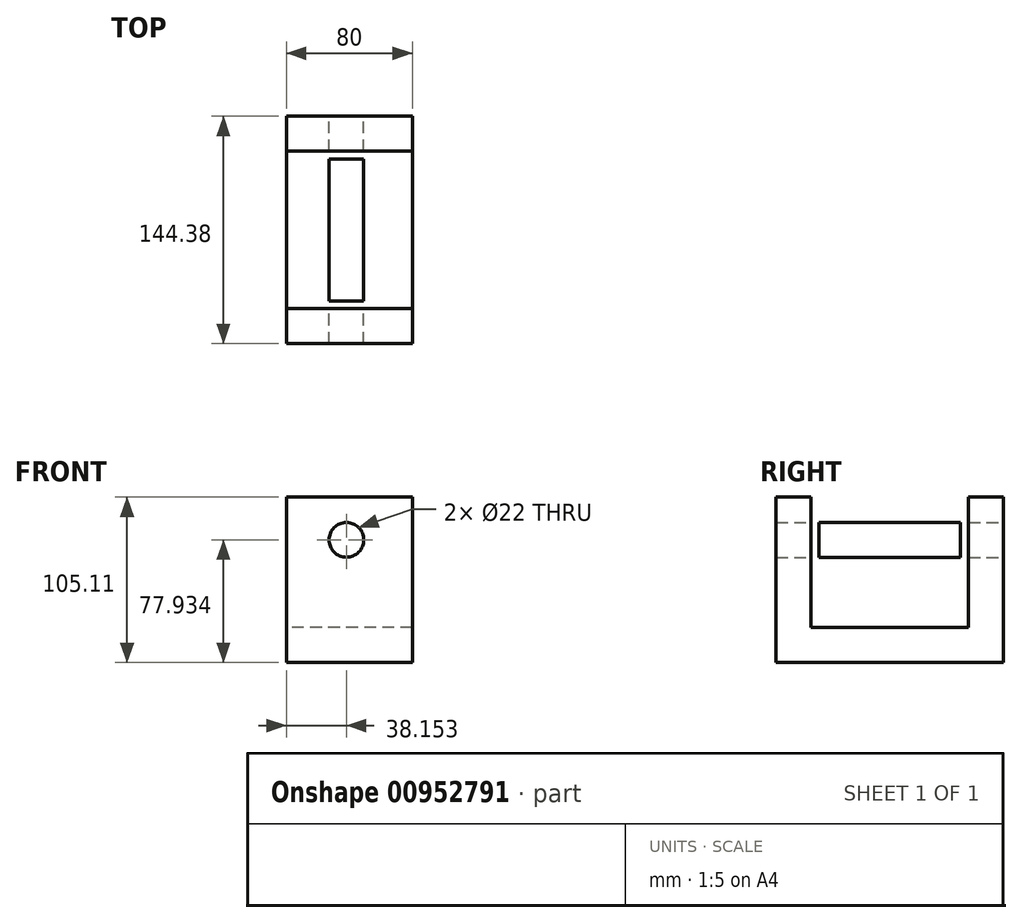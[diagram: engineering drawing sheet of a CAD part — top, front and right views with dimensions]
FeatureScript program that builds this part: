
annotation { "Feature Type Name" : "Feature", "Feature Type Description" : "" }
export const myFeature = defineFeature(function(context is Context, id is Id, definition is map)
    precondition{}
    {
        {
            var Q0;
            Q0=qCreatedBy(makeId("Right.planeOp"),FACE);
            var sketch = newSketch(context, id + "F0", { "sketchPlane" : qUnion([Q0])});
            skLineSegment(sketch, "E0", {"start": v(0, 0) * mm, "end": v(0, 85.7) * mm, "construction": true});
            skLineSegment(sketch, "E1", {"start": v(-50, 50.82) * mm, "end": v(-50, -32.1) * mm});
            skLineSegment(sketch, "E2.MirrorCS", {"start": v(50, 50.82) * mm, "end": v(50, -32.1) * mm});
            skLineSegment(sketch, "E3", {"start": v(-50, -32.1) * mm, "end": v(50, -32.1) * mm});
            skLineSegment(sketch, "E4.0", {"start": v(72.19, 50.82) * mm, "end": v(72.19, -54.3) * mm});
            skLineSegment(sketch, "E4.1", {"start": v(-72.19, -54.3) * mm, "end": v(72.19, -54.3) * mm});
            skLineSegment(sketch, "E4.2", {"start": v(-72.19, 50.82) * mm, "end": v(-72.19, -54.3) * mm});
            skLineSegment(sketch, "E5", {"start": v(-50, 50.82) * mm, "end": v(-72.19, 50.82) * mm});
            skLineSegment(sketch, "E6", {"start": v(50, 50.82) * mm, "end": v(72.19, 50.82) * mm});
            skSolve(sketch);
        }
        {
            var Q0;
            Q0=makeQuery(id+"F0.imprint","IMPRINT",FACE,{"disambiguationData":[TD([[makeQuery(id+"F0.imprint","IMPRINT",EDGE,{"derivedFrom":sQuery(id+"F0.wireOp",EDGE,"E1")}),-1.0]])]});
            extrude(context, id + "F1", {"entities" : qUnion([Q0]), "depth" : 80 * mm, "offsetDistance" : 25 * mm});
        }
        {
            var Q0;
            Q0=qCreatedBy(makeId("Front.planeOp"),FACE);
            var sketch = newSketch(context, id + "F2", { "sketchPlane" : qUnion([Q0])});
            skCircle(sketch, "E7", {"center": v(38.15, 23.64) * mm, "radius": 11 * mm});
            skSolve(sketch);
        }
        {
            var Q0;
            Q0=qSketchRegion(id+"F2",true);
            extrude(context, id + "F3", {"entities" : qUnion([Q0]), "operationType" : NewBodyOperationType.REMOVE, "endBound" : BoundingType.SYMMETRIC, "depth" : 150 * mm, "offsetDistance" : 25 * mm});
        }
        {
            var Q0;
            Q0=qSketchRegion(id+"F2",true);
            extrude(context, id + "F4", {"entities" : qUnion([Q0]), "endBound" : BoundingType.SYMMETRIC, "depth" : 90 * mm, "offsetDistance" : 25 * mm});
        }
    });
